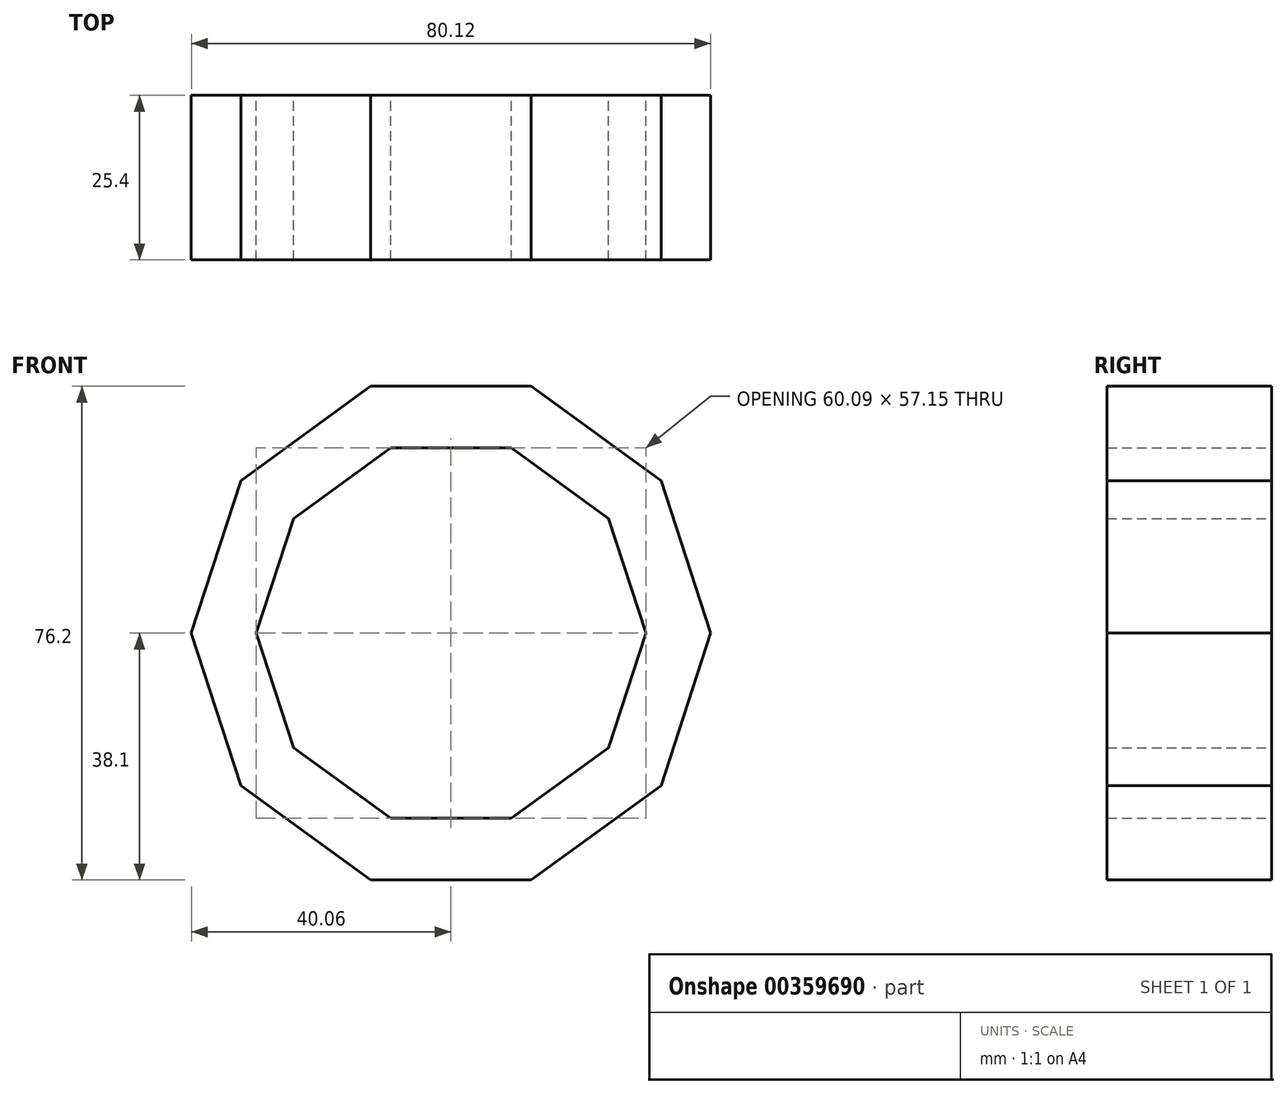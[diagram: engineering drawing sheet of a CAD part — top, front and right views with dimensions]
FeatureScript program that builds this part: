
annotation { "Feature Type Name" : "Feature", "Feature Type Description" : "" }
export const myFeature = defineFeature(function(context is Context, id is Id, definition is map)
    precondition{}
    {
        {
            var Q0;
            Q0=qCreatedBy(makeId("Front.planeOp"),FACE);
            var sketch = newSketch(context, id + "F0", { "sketchPlane" : qUnion([Q0])});
            skLineSegment(sketch, "E0", {"start": v(0, 0) * mm, "end": v(0, 38.1) * mm});
            skCircle(sketch, "E1.cCircle", {"center": v(0, 0) * mm, "radius": 38.1 * mm, "construction": true});
            skLineSegment(sketch, "E1.0", {"start": v(-12.38, 38.1) * mm, "end": v(12.38, 38.1) * mm});
            skLineSegment(sketch, "E1.1", {"start": v(12.38, 38.1) * mm, "end": v(32.4, 23.55) * mm});
            skLineSegment(sketch, "E1.2", {"start": v(32.4, 23.55) * mm, "end": v(40.06, 0) * mm});
            skLineSegment(sketch, "E1.3", {"start": v(40.06, 0) * mm, "end": v(32.4, -23.55) * mm});
            skLineSegment(sketch, "E1.4", {"start": v(32.4, -23.55) * mm, "end": v(12.38, -38.1) * mm});
            skLineSegment(sketch, "E1.5", {"start": v(12.38, -38.1) * mm, "end": v(-12.38, -38.1) * mm});
            skLineSegment(sketch, "E1.6", {"start": v(-12.38, -38.1) * mm, "end": v(-32.4, -23.55) * mm});
            skLineSegment(sketch, "E1.7", {"start": v(-32.4, -23.55) * mm, "end": v(-40.06, 0) * mm});
            skLineSegment(sketch, "E1.8", {"start": v(-40.06, 0) * mm, "end": v(-32.4, 23.55) * mm});
            skLineSegment(sketch, "E1.9", {"start": v(-32.4, 23.55) * mm, "end": v(-12.38, 38.1) * mm});
            skPoint(sketch, "E1.0.midPoint", {"position": v(0, 38.1) * mm});
            skLineSegment(sketch, "E2", {"start": v(0, 0) * mm, "end": v(0, 28.58) * mm});
            skPoint(sketch, "E3.0.midPoint", {"position": v(0, 28.58) * mm});
            skCircle(sketch, "E4.cCircle", {"center": v(0, 0) * mm, "radius": 28.58 * mm, "construction": true});
            skLineSegment(sketch, "E4.0", {"start": v(-9.28, 28.58) * mm, "end": v(9.28, 28.58) * mm});
            skLineSegment(sketch, "E4.1", {"start": v(9.28, 28.58) * mm, "end": v(24.3, 17.66) * mm});
            skLineSegment(sketch, "E4.2", {"start": v(24.3, 17.66) * mm, "end": v(30.05, 0) * mm});
            skLineSegment(sketch, "E4.3", {"start": v(30.05, 0) * mm, "end": v(24.3, -17.66) * mm});
            skLineSegment(sketch, "E4.4", {"start": v(24.3, -17.66) * mm, "end": v(9.28, -28.58) * mm});
            skLineSegment(sketch, "E4.5", {"start": v(9.28, -28.58) * mm, "end": v(-9.28, -28.58) * mm});
            skLineSegment(sketch, "E4.6", {"start": v(-9.28, -28.58) * mm, "end": v(-24.3, -17.66) * mm});
            skLineSegment(sketch, "E4.7", {"start": v(-24.3, -17.66) * mm, "end": v(-30.05, 0) * mm});
            skLineSegment(sketch, "E4.8", {"start": v(-30.05, 0) * mm, "end": v(-24.3, 17.66) * mm});
            skLineSegment(sketch, "E4.9", {"start": v(-24.3, 17.66) * mm, "end": v(-9.28, 28.58) * mm});
            skSolve(sketch);
        }
        {
            var Q0;
            Q0 = qSketchRegion(id + "F0", true);
            extrude(context, id + "F1", {"entities" : qUnion([Q0]), "depth" : 25.4 * mm});
        }
    });
